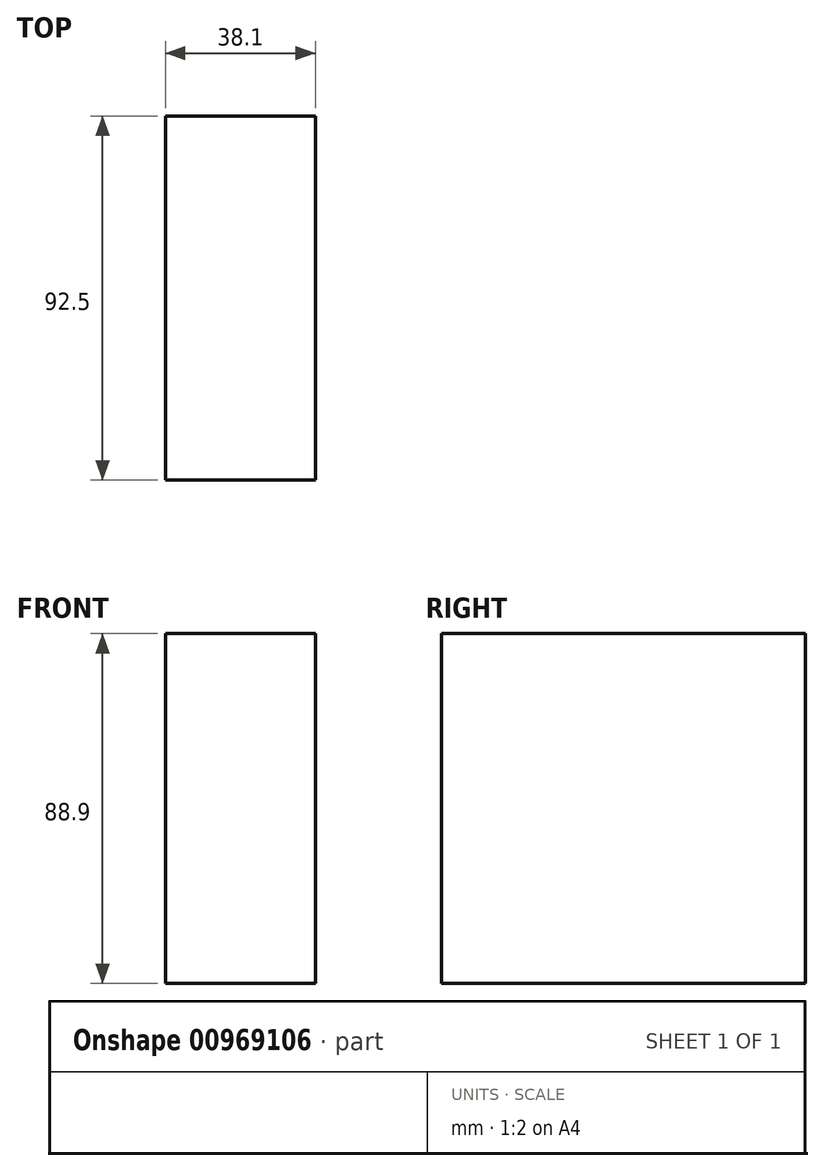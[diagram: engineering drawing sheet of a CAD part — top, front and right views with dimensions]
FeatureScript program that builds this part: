
annotation { "Feature Type Name" : "Feature", "Feature Type Description" : "" }
export const myFeature = defineFeature(function(context is Context, id is Id, definition is map)
    precondition{}
    {
        {
            assignVariable(context, id + "F0", {"name" : "length", "anyValue" : 92.5});
        }
        {
            var Q0;
            Q0=qCreatedBy(makeId("Front.planeOp"),FACE);
            var sketch = newSketch(context, id + "F1", { "sketchPlane" : qUnion([Q0])});
            skLineSegment(sketch, "E0.bottom", {"start": v(0, 0) * mm, "end": v(38.1, 0) * mm});
            skLineSegment(sketch, "E0.top", {"start": v(0, 88.9) * mm, "end": v(38.1, 88.9) * mm});
            skLineSegment(sketch, "E0.left", {"start": v(0, 0) * mm, "end": v(0, 88.9) * mm});
            skLineSegment(sketch, "E0.right", {"start": v(38.1, 0) * mm, "end": v(38.1, 88.9) * mm});
            skSolve(sketch);
        }
        {
            var Q0;
            Q0=makeQuery(id+"F1.imprint","IMPRINT",FACE,{"disambiguationData":[TD([[makeQuery(id+"F1.imprint","IMPRINT",EDGE,{"derivedFrom":sQuery(id+"F1.wireOp",EDGE,"E0.bottom")}),1.0]])]});
            extrude(context, id + "F2", {"entities" : qUnion([Q0]), "depth" : (getVariable(context, 'length')) * mm, "offsetDistance" : 25.4 * mm});
        }
    });
